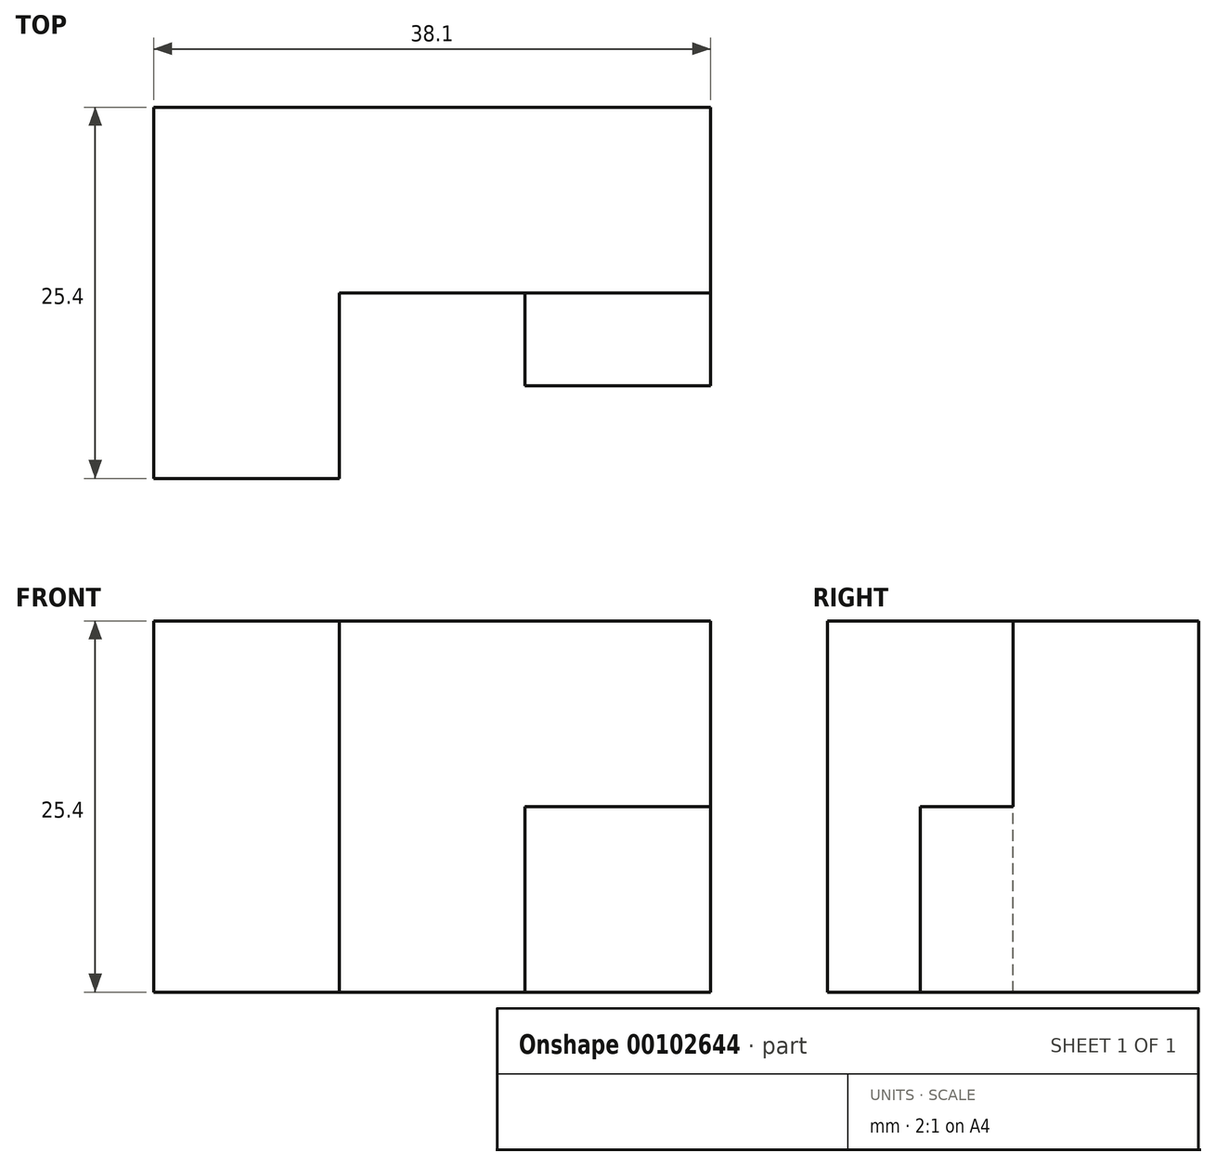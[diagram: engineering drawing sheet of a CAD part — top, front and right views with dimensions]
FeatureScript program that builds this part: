
annotation { "Feature Type Name" : "Feature", "Feature Type Description" : "" }
export const myFeature = defineFeature(function(context is Context, id is Id, definition is map)
    precondition{}
    {
        {
            var Q0;
            Q0=qCreatedBy(makeId("Top.planeOp"),FACE);
            var sketch = newSketch(context, id + "F0", { "sketchPlane" : qUnion([Q0])});
            skLineSegment(sketch, "E0", {"start": v(0, 0) * mm, "end": v(-12.7, 0) * mm});
            skLineSegment(sketch, "E1", {"start": v(-12.7, 0) * mm, "end": v(-12.7, 25.4) * mm});
            skLineSegment(sketch, "E2", {"start": v(-12.7, 25.4) * mm, "end": v(25.4, 25.4) * mm});
            skLineSegment(sketch, "E3", {"start": v(25.4, 25.4) * mm, "end": v(25.4, 0) * mm});
            skLineSegment(sketch, "E4", {"start": v(25.4, 0) * mm, "end": v(12.7, 0) * mm});
            skLineSegment(sketch, "E5", {"start": v(12.7, 0) * mm, "end": v(12.7, 12.7) * mm});
            skLineSegment(sketch, "E6", {"start": v(12.7, 12.7) * mm, "end": v(0, 12.7) * mm});
            skLineSegment(sketch, "E7", {"start": v(0, 12.7) * mm, "end": v(0, 0) * mm});
            skLineSegment(sketch, "E8", {"start": v(0, 0) * mm, "end": v(12.7, 0) * mm});
            skSolve(sketch);
        }
        {
            var Q0;
            Q0 = qSketchRegion(id + "F0", true);
            extrude(context, id + "F1", {"entities" : qUnion([Q0]), "endBound" : BoundingType.SYMMETRIC, "depth" : 25.4 * mm});
        }
        {
            var Q0;
            Q0=makeQuery(id+"F1.opExtrude","CAP_FACE",FACE,{"disambiguationData":[OSD([sQuery(id+"F0.wireOp",EDGE,"E0"),sQuery(id+"F0.wireOp",EDGE,"E1"),sQuery(id+"F0.wireOp",EDGE,"E2"),sQuery(id+"F0.wireOp",EDGE,"E3"),sQuery(id+"F0.wireOp",EDGE,"E4"),sQuery(id+"F0.wireOp",EDGE,"E8")])],"isStart":false});
            var sketch = newSketch(context, id + "F2", { "sketchPlane" : qUnion([Q0])});
            skLineSegment(sketch, "E9", {"start": v(0, 0) * mm, "end": v(0, 12.7) * mm});
            skLineSegment(sketch, "E10", {"start": v(0, 12.7) * mm, "end": v(12.7, 12.7) * mm});
            skLineSegment(sketch, "E11", {"start": v(12.7, 12.7) * mm, "end": v(12.7, 0) * mm});
            skSolve(sketch);
        }
        {
            var Q0;
            {var subQ0=sQuery(id+"F2.wireOp",EDGE,"E9");Q0=makeQuery(id+"F2.imprint","IMPRINT",FACE,{"disambiguationData":[TD([[makeQuery(id+"F2.imprint","IMPRINT",EDGE,{"derivedFrom":subQ0}),-1.0]])]});}
            extrude(context, id + "F3", {"entities" : qUnion([Q0]), "operationType" : NewBodyOperationType.REMOVE, "endBound" : BoundingType.THROUGH_ALL, "oppositeDirection" : true, "depth" : 25.4 * mm});
        }
        {
            var Q0;
            Q0=makeQuery(id+"F3.boolean.opBoolean","COPY",FACE,{"derivedFrom":makeQuery(id+"F3.opExtrude","SWEPT_FACE",FACE,{"disambiguationData":[OSD([sQuery(id+"F2.wireOp",EDGE,"E11")])]})});
            var sketch = newSketch(context, id + "F4", { "sketchPlane" : qUnion([Q0])});
            skLineSegment(sketch, "E12", {"start": v(-12.7, 0) * mm, "end": v(0, 0) * mm});
            skSolve(sketch);
        }
        {
            var Q0;
            {var subQ0=sQuery(id+"F4.wireOp",EDGE,"E12");Q0=makeQuery(id+"F4.imprint","IMPRINT",FACE,{"disambiguationData":[TD([[makeQuery(id+"F4.imprint","IMPRINT",EDGE,{"derivedFrom":subQ0}),1.0]])]});}
            extrude(context, id + "F5", {"entities" : qUnion([Q0]), "operationType" : NewBodyOperationType.REMOVE, "endBound" : BoundingType.THROUGH_ALL, "oppositeDirection" : true, "depth" : 25.4 * mm});
        }
        {
            var Q0;
            Q0=makeQuery(id+"F5.boolean.opBoolean","COPY",FACE,{"derivedFrom":makeQuery(id+"F5.opExtrude","SWEPT_FACE",FACE,{"disambiguationData":[OSD([sQuery(id+"F4.wireOp",EDGE,"E12")])]})});
            var sketch = newSketch(context, id + "F6", { "sketchPlane" : qUnion([Q0])});
            skLineSegment(sketch, "E13", {"start": v(12.7, 6.35) * mm, "end": v(25.4, 6.35) * mm});
            skSolve(sketch);
        }
        {
            var Q0;
            {var subQ0=sQuery(id+"F6.wireOp",EDGE,"E13");Q0=makeQuery(id+"F6.imprint","IMPRINT",FACE,{"disambiguationData":[TD([[makeQuery(id+"F6.imprint","IMPRINT",EDGE,{"derivedFrom":subQ0}),-1.0]])]});}
            extrude(context, id + "F7", {"entities" : qUnion([Q0]), "operationType" : NewBodyOperationType.REMOVE, "endBound" : BoundingType.THROUGH_ALL, "oppositeDirection" : true, "depth" : 25.4 * mm});
        }
    });
